# Revit family: CER
name_source: partatom
category: Lighting Fixtures
revit_build: Autodesk Revit MEP 2012 (Build: 20110309_2315(x64)
units: mm (PartAtom-declared; Revit-internal decimal feet)

## types (1)
- CER
    Apparent Load = 0 VA
    Color Filter = 16777215
    Default Elevation = 48.000"
    Description = CE - LED Emergency Exit
    Dimming Lamp Color Temperature Shift = <None>
    Emit Shape Visible in Rendering = No
    Emit from Rectangle Length = 10.000"
    Emit from Rectangle Width = 5.000"
    Finish = Hubbell - White
    Glass = Hubbell - light Glass
    Lamp = LED Lamp
    Lens = Hubbell - Red Glass
    Load Classification = Lighting
    Manufacturer = Compass Lighting
    Manufacturer Fax = (866)-898-0131
    Model = CER
    Photometric Web File = generic
    Product Documentation Link = http://cdn.compasslightingproducts.com
    Product Page URL = http://www.compasslightingproducts.com
    Tilt Angle = 0.00°
    URL = http://www.compasslightingproducts.com
    Voltage = 120 V
    Wattage Comments = 1.78 - 1.88 W

## geometry (parser evidence)
native form markers: Sweep x2
no freeform markers — native parametric forms only
